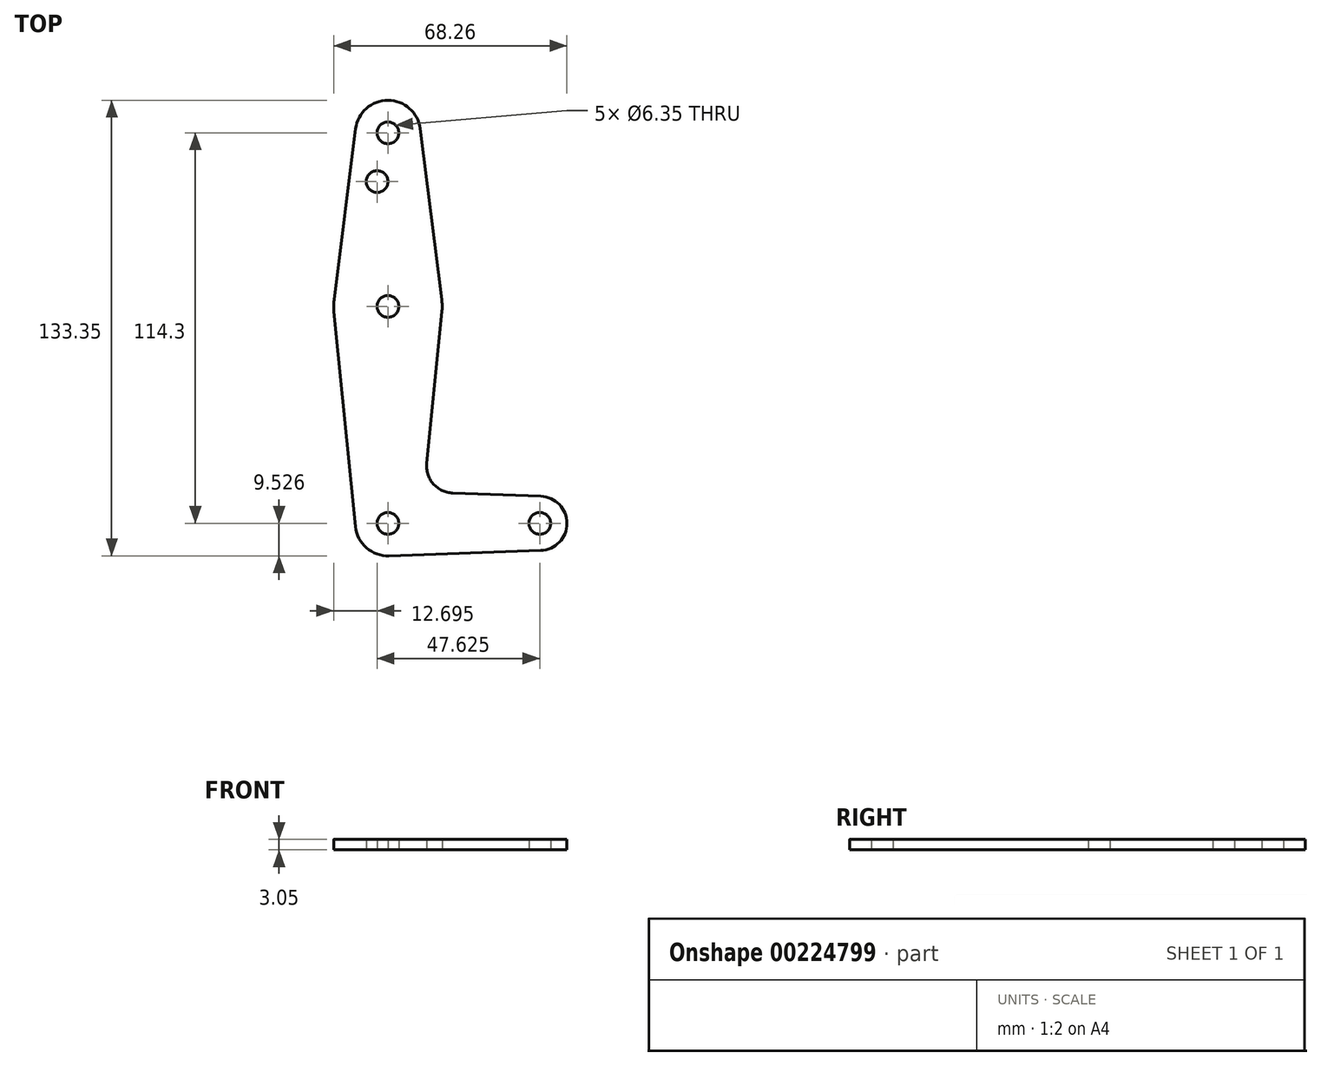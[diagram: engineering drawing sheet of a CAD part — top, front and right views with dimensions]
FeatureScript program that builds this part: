
annotation { "Feature Type Name" : "Feature", "Feature Type Description" : "" }
export const myFeature = defineFeature(function(context is Context, id is Id, definition is map)
    precondition{}
    {
        {
            var Q0;
            Q0=qCreatedBy(makeId("Top.planeOp"),FACE);
            var sketch = newSketch(context, id + "F0", { "sketchPlane" : qUnion([Q0])});
            skLineSegment(sketch, "E0", {"start": v(0, 50.4) * mm, "end": v(0, -63.9) * mm, "construction": true});
            skLineSegment(sketch, "E1", {"start": v(0, -63.9) * mm, "end": v(44.45, -63.9) * mm, "construction": true});
            skCircle(sketch, "E2", {"center": v(0, 50.4) * mm, "radius": 9.53 * mm});
            skCircle(sketch, "E3", {"center": v(0, -0.4) * mm, "radius": 15.88 * mm});
            skCircle(sketch, "E4", {"center": v(0, -63.9) * mm, "radius": 9.53 * mm});
            skCircle(sketch, "E5", {"center": v(44.45, -63.9) * mm, "radius": 7.94 * mm});
            skCircle(sketch, "E6", {"center": v(0, 50.4) * mm, "radius": 3.18 * mm});
            skCircle(sketch, "E7", {"center": v(0, -0.4) * mm, "radius": 3.18 * mm});
            skCircle(sketch, "E8", {"center": v(0, -63.9) * mm, "radius": 3.18 * mm});
            skCircle(sketch, "E9", {"center": v(44.45, -63.9) * mm, "radius": 3.18 * mm});
            skLineSegment(sketch, "E10", {"start": v(0, 25) * mm, "end": v(-3.17, 25) * mm});
            skLineSegment(sketch, "E11", {"start": v(-3.17, 25) * mm, "end": v(-3.17, 36.13) * mm});
            skCircle(sketch, "E12", {"center": v(-3.17, 36.13) * mm, "radius": 3.18 * mm});
            skLineSegment(sketch, "E13", {"start": v(-9.45, 51.6) * mm, "end": v(-15.75, 1.6) * mm});
            skLineSegment(sketch, "E14", {"start": v(9.45, 51.6) * mm, "end": v(15.75, 1.6) * mm});
            skLineSegment(sketch, "E15", {"start": v(-15.8, -1.98) * mm, "end": v(-9.48, -64.85) * mm});
            skLineSegment(sketch, "E16", {"start": v(15.8, -1.98) * mm, "end": v(11.34, -46.3) * mm});
            skLineSegment(sketch, "E17", {"start": v(0.34, -73.41) * mm, "end": v(44.73, -71.83) * mm});
            skLineSegment(sketch, "E18", {"start": v(44.73, -55.96) * mm, "end": v(18.97, -55.04) * mm});
            skArc(sketch, "E19.filletArc", {"start": v(11.34, -46.3) * mm, "mid": v(13.26, -52.32) * mm, "end": v(18.97, -55.04) * mm});
            skSolve(sketch);
        }
        {
            var Q0;
            Q0 = qSketchRegion(id + "F0", true);
            extrude(context, id + "F1", {"entities" : qUnion([Q0]), "depth" : 3.05 * mm});
        }
    });
